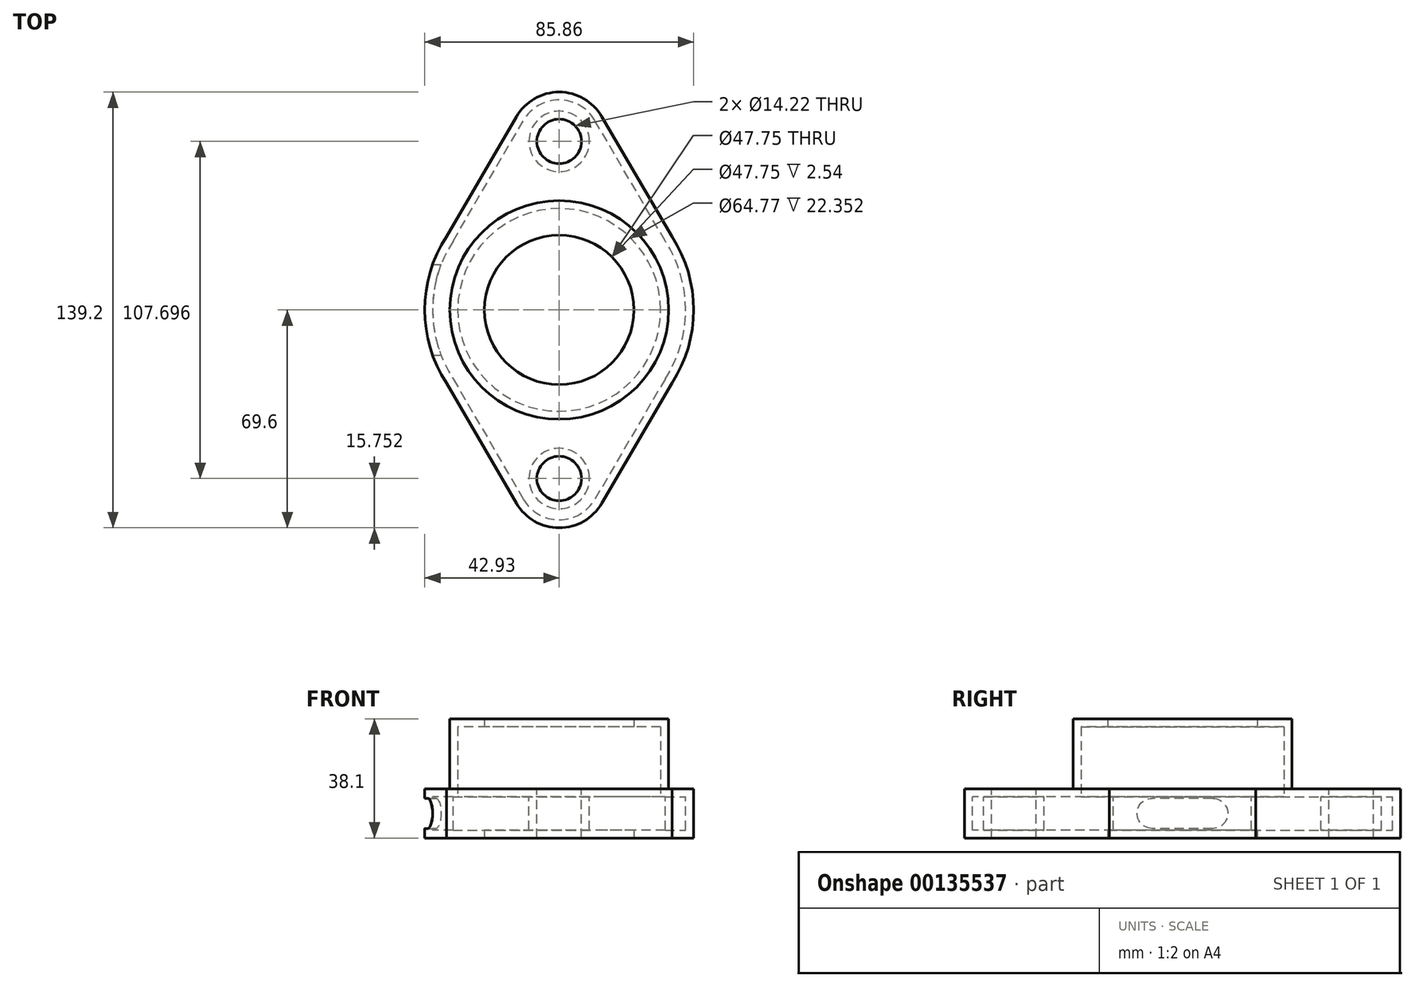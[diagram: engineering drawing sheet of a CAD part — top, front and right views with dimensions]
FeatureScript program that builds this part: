
annotation { "Feature Type Name" : "Feature", "Feature Type Description" : "" }
export const myFeature = defineFeature(function(context is Context, id is Id, definition is map)
    precondition{}
    {
        {
            var Q0;
            Q0=qCreatedBy(makeId("Top.planeOp"),FACE);
            var sketch = newSketch(context, id + "F0", { "sketchPlane" : qUnion([Q0])});
            skCircle(sketch, "E0", {"center": v(0, 0) * mm, "radius": 34.93 * mm});
            skCircle(sketch, "E1", {"center": v(0, 53.85) * mm, "radius": 7.11 * mm});
            skCircle(sketch, "E2.MirrorC", {"center": v(0, -53.85) * mm, "radius": 7.11 * mm});
            skCircle(sketch, "E3", {"center": v(0, 0) * mm, "radius": 23.88 * mm});
            skCircle(sketch, "E4", {"center": v(0, 0) * mm, "radius": 28.58 * mm});
            skArc(sketch, "E5", {"start": v(-36, 23.38) * mm, "mid": v(-42.93, 0) * mm, "end": v(-36, -23.38) * mm});
            skArc(sketch, "E6.trimOffspring", {"start": v(36, -23.38) * mm, "mid": v(42.93, 0) * mm, "end": v(36, 23.38) * mm});
            skArc(sketch, "E7", {"start": v(13.6, 61.78) * mm, "mid": v(0, 69.6) * mm, "end": v(-13.6, 61.78) * mm});
            skArc(sketch, "E8.MirrorC", {"start": v(13.6, -61.78) * mm, "mid": v(0, -69.6) * mm, "end": v(-13.6, -61.78) * mm});
            skLineSegment(sketch, "E9", {"start": v(-36, 23.38) * mm, "end": v(-13.6, 61.78) * mm});
            skLineSegment(sketch, "E10.MirrorCS", {"start": v(36, 23.38) * mm, "end": v(13.6, 61.78) * mm});
            skLineSegment(sketch, "E11.MirrorCS", {"start": v(-36, -23.38) * mm, "end": v(-13.6, -61.78) * mm});
            skLineSegment(sketch, "E12.MirrorCS", {"start": v(36, -23.38) * mm, "end": v(13.6, -61.78) * mm});
            skSolve(sketch);
        }
        {
            var Q0;
            Q0=makeQuery(id+"F0.imprint","IMPRINT",FACE,{"disambiguationData":[TD([[makeQuery(id+"F0.imprint","IMPRINT",EDGE,{"derivedFrom":sQuery(id+"F0.wireOp",EDGE,"E0")}),1.0]])]});
            var Q1;
            Q1=makeQuery(id+"F0.imprint","IMPRINT",FACE,{"disambiguationData":[TD([[makeQuery(id+"F0.imprint","IMPRINT",EDGE,{"derivedFrom":sQuery(id+"F0.wireOp",EDGE,"E3")}),-1.0]])]});
            extrude(context, id + "F1", {"entities" : qUnion([Q0, Q1]), "depth" : 22.35 * mm});
        }
        {
            var Q0;
            Q0=makeQuery(id+"F0.imprint","IMPRINT",FACE,{"disambiguationData":[TD([[makeQuery(id+"F0.imprint","IMPRINT",EDGE,{"derivedFrom":sQuery(id+"F0.wireOp",EDGE,"E0")}),-1.0]])]});
            var Q1;
            Q1=makeQuery(id+"F0.imprint","IMPRINT",FACE,{"disambiguationData":[TD([[makeQuery(id+"F0.imprint","IMPRINT",EDGE,{"derivedFrom":sQuery(id+"F0.wireOp",EDGE,"E3")}),-1.0]])]});
            var Q2;
            Q2=makeQuery(id+"F0.imprint","IMPRINT",FACE,{"disambiguationData":[TD([[makeQuery(id+"F0.imprint","IMPRINT",EDGE,{"derivedFrom":sQuery(id+"F0.wireOp",EDGE,"E0")}),1.0]])]});
            extrude(context, id + "F2", {"entities" : qUnion([Q0, Q1, Q2]), "operationType" : NewBodyOperationType.ADD, "oppositeDirection" : true, "depth" : 15.75 * mm});
        }
        {
            var Q0;
            Q0=makeQuery(id+"F2.opExtrude","SWEPT_FACE",FACE,{"disambiguationData":[OSD([sQuery(id+"F0.wireOp",EDGE,"E3")])]});
            var Q1;
            Q1=makeQuery(id+"F1.opExtrude","SWEPT_FACE",FACE,{"disambiguationData":[OSD([sQuery(id+"F0.wireOp",EDGE,"E3")])]});
            var Q2;
            Q2=makeQuery(id+"F2.opExtrude","SWEPT_BODY",BODY,{"disambiguationData":[OSD([sQuery(id+"F0.wireOp",EDGE,"E1"),sQuery(id+"F0.wireOp",EDGE,"E2.MirrorC"),sQuery(id+"F0.wireOp",EDGE,"E3"),sQuery(id+"F0.wireOp",EDGE,"E5"),sQuery(id+"F0.wireOp",EDGE,"E6.trimOffspring"),sQuery(id+"F0.wireOp",EDGE,"E7"),sQuery(id+"F0.wireOp",EDGE,"E8.MirrorC"),sQuery(id+"F0.wireOp",EDGE,"E9"),sQuery(id+"F0.wireOp",EDGE,"E10.MirrorCS"),sQuery(id+"F0.wireOp",EDGE,"E11.MirrorCS"),sQuery(id+"F0.wireOp",EDGE,"E12.MirrorCS")])]});
            var Q3;
            Q3=makeQuery(id+"F1.opExtrude","SWEPT_BODY",BODY,{"disambiguationData":[OSD([sQuery(id+"F0.wireOp",EDGE,"E0"),sQuery(id+"F0.wireOp",EDGE,"E3")])]});
            shell(context, id + "F3", {"entities" : qUnion([Q0, Q1]), "parts" : qUnion([Q2, Q3]), "thickness" : 2.54 * mm});
        }
        {
            var Q0;
            Q0=qCreatedBy(makeId("Right.planeOp"),FACE);
            var sketch = newSketch(context, id + "F4", { "sketchPlane" : qUnion([Q0])});
            skArc(sketch, "E13", {"start": v(9.65, -12.7) * mm, "mid": v(14.48, -7.87) * mm, "end": v(9.65, -3.05) * mm});
            skArc(sketch, "E14.MirrorC", {"start": v(-9.65, -12.7) * mm, "mid": v(-14.48, -7.87) * mm, "end": v(-9.65, -3.05) * mm});
            skLineSegment(sketch, "E15", {"start": v(9.65, -12.7) * mm, "end": v(-9.65, -12.7) * mm});
            skLineSegment(sketch, "E16", {"start": v(9.65, -3.05) * mm, "end": v(-9.65, -3.05) * mm});
            skSolve(sketch);
        }
        {
            var Q0;
            Q0 = qSketchRegion(id + "F4", true);
            extrude(context, id + "F5", {"entities" : qUnion([Q0]), "operationType" : NewBodyOperationType.REMOVE, "endBound" : BoundingType.THROUGH_ALL, "oppositeDirection" : true, "depth" : 57.47 * mm});
        }
    });
